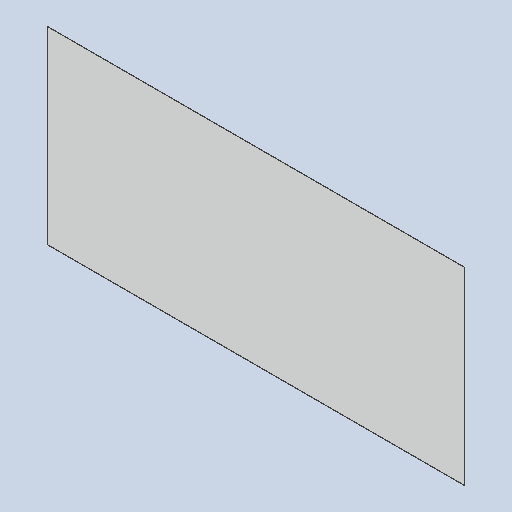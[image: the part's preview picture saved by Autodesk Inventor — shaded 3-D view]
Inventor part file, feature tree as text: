
AUTODESK INVENTOR PART (.ipt)
format: ipt  version: 2023 (Build 270158000, 158)  size: 86,016 bytes
history: native  units: mm
features: extrude x1, sketch x1
ambient origin geometry x8: Origin, YZ Plane, XZ Plane, XY Plane, X Axis, Y Axis, Z Axis, Center Point
bodies: Solid1 (feature_tree)
feature tree (2):
  extrude  "Extrusion1"  Depth=1160.0mm
  sketch  "Sketch1"  dims[d0=2560.0mm d1=1160.0mm d2=2.0mm d3=0.0mm]
